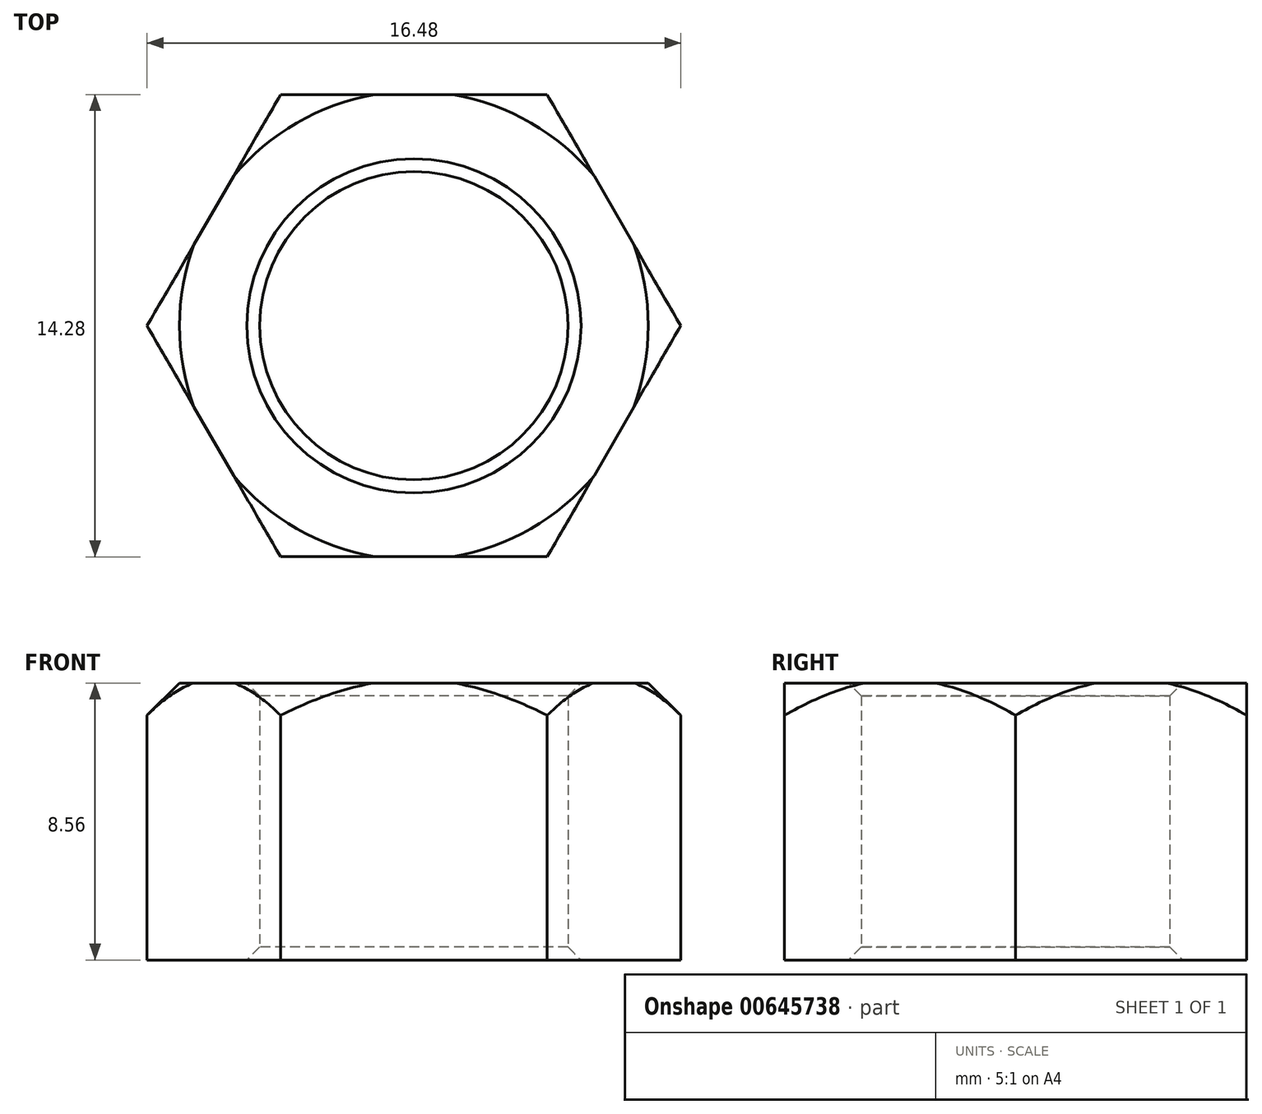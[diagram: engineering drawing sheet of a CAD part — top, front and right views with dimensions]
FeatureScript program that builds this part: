
annotation { "Feature Type Name" : "Feature", "Feature Type Description" : "" }
export const myFeature = defineFeature(function(context is Context, id is Id, definition is map)
    precondition{}
    {
        {
            var Q0;
            Q0=qCreatedBy(makeId("Top.planeOp"),FACE);
            var sketch = newSketch(context, id + "F0", { "sketchPlane" : qUnion([Q0])});
            skCircle(sketch, "E0.cCircle", {"center": v(0, 0) * mm, "radius": 7.13 * mm, "construction": true});
            skLineSegment(sketch, "E0.0", {"start": v(-4.12, 7.13) * mm, "end": v(4.12, 7.13) * mm});
            skLineSegment(sketch, "E0.1", {"start": v(4.12, 7.14) * mm, "end": v(8.24, 0) * mm});
            skLineSegment(sketch, "E0.2", {"start": v(8.24, 0) * mm, "end": v(4.12, -7.13) * mm});
            skLineSegment(sketch, "E0.3", {"start": v(4.12, -7.13) * mm, "end": v(-4.12, -7.14) * mm});
            skLineSegment(sketch, "E0.4", {"start": v(-4.12, -7.14) * mm, "end": v(-8.24, 0) * mm});
            skLineSegment(sketch, "E0.5", {"start": v(-8.24, 0) * mm, "end": v(-4.12, 7.14) * mm});
            skPoint(sketch, "E0.0.midPoint", {"position": v(0, 7.13) * mm});
            skCircle(sketch, "E1", {"center": v(0, 0) * mm, "radius": 4.76 * mm});
            skSolve(sketch);
        }
        {
            var Q0;
            Q0=makeQuery(id+"F0.imprint","IMPRINT",FACE,{"disambiguationData":[TD([[makeQuery(id+"F0.imprint","IMPRINT",EDGE,{"derivedFrom":sQuery(id+"F0.wireOp",EDGE,"E0.0")}),-1.0]])]});
            extrude(context, id + "F1", {"entities" : qUnion([Q0]), "depth" : 8.56 * mm, "offsetDistance" : 25 * mm});
        }
        {
            var Q0;
            Q0=makeQuery(id+"F1.opExtrude","CAP_EDGE",EDGE,{"disambiguationData":[OSD([sQuery(id+"F0.wireOp",EDGE,"E1")])],"isStart":false});
            var Q1;
            Q1=makeQuery(id+"F1.opExtrude","CAP_EDGE",EDGE,{"disambiguationData":[OSD([sQuery(id+"F0.wireOp",EDGE,"E1")])],"isStart":true});
            chamfer(context, id + "F2", {"entities" : qUnion([Q0, Q1]), "chamferType" : ChamferType.OFFSET_ANGLE, "width" : .4 * mm, "oppositeDirection" : false, "angle" : 45 * degree, "tangentPropagation" : true});
        }
        {
            var Q0;
            Q0=qCreatedBy(makeId("Front.planeOp"),FACE);
            var sketch = newSketch(context, id + "F3", { "sketchPlane" : qUnion([Q0])});
            skLineSegment(sketch, "E2", {"start": v(7.24, 8.56) * mm, "end": v(8.24, 7.56) * mm});
            skLineSegment(sketch, "E3", {"start": v(8.24, 7.56) * mm, "end": v(8.24, 8.56) * mm});
            skLineSegment(sketch, "E4", {"start": v(8.24, 8.56) * mm, "end": v(7.24, 8.56) * mm});
            skSolve(sketch);
        }
        {
            var Q0;
            Q0 = qSketchRegion(id + "F3", true);
            var Q1;
            {var subQ0=sQuery(id+"F0.wireOp",EDGE,"E1");Q1=makeQuery(id+"F2.opChamfer","BLEND_EDGE",EDGE,{"blendedFrom":[makeQuery(id+"F1.opExtrude","CAP_EDGE",EDGE,{"disambiguationData":[OSD([subQ0])],"isStart":false}),makeQuery(id+"F1.opExtrude","SWEPT_FACE",FACE,{"disambiguationData":[OSD([subQ0])]})],"blendedInto":[makeQuery(id+"F1.opExtrude","SWEPT_FACE",FACE,{"disambiguationData":[OSD([subQ0])]})]});}
            revolve(context, id + "F4", {"operationType" : NewBodyOperationType.REMOVE, "entities" : qUnion([Q0]), "axis" : qUnion([Q1]), "revolveType" : RevolveType.FULL, "oppositeDirection" : true});
        }
        {
            var Q0;
            Q0=makeQuery(id+"F1.opExtrude","CAP_FACE",FACE,{"disambiguationData":[OSD([sQuery(id+"F0.wireOp",EDGE,"E0.0"),sQuery(id+"F0.wireOp",EDGE,"E0.1"),sQuery(id+"F0.wireOp",EDGE,"E0.2"),sQuery(id+"F0.wireOp",EDGE,"E0.3"),sQuery(id+"F0.wireOp",EDGE,"E0.4"),sQuery(id+"F0.wireOp",EDGE,"E0.5"),sQuery(id+"F0.wireOp",EDGE,"E1")])],"isStart":false});
            cPlane(context, id + "F5", {"entities" : qUnion([Q0]), "cplaneType" : CPlaneType.OFFSET, "offset" : (8.56 / 2) * mm, "oppositeDirection" : true, "width" : 150 * mm, "height" : 150 * mm});
        }
    });
